# Revit family: Prises non verrouilllées 250 V
name_source: partatom
category: Installations électriques
revit_build: Autodesk Revit 2018 (Build: 20170223_1515(x64)
units: mm (PartAtom-declared; Revit-internal decimal feet)

## family parameters
Conserver l'orientation des annotations = Non
Cote de connecteur circulaire = Utiliser le diamètre
Couper avec des vides une fois chargée = Non
Hôte = Face
Partagée = Non
Point de calcul de pièce = Non
Type d'élément = Normal

## types (9) — shared parameters
Elévation par défaut = 1000 mm  [stored 3.28084 ft]
Fabricant = Legrand
Famille produit = 0854-P17 TEMPRA PRO
Intensité A = 16 A
Prise au standard international pour montage encastré ou saillie avec accessoire permet la connexion d'appareils de puissance = Prise à usage domestique
Température maximum d'utilisation = 40
Température minimum d'utilisation = -25
classe de protection IP = IP54
installation Encastrée E ou Saillie S = encastré
matériau du boitier = plastique
profondeur d'encastrement mm = 26 mm
profondeur mm = 43 mm  [stored 0.141076 ft]
résistance aux chocs IK = 8
sans halogène = Oui
type de raccordement = bornes à vis
zero-valued in all types: Position de la Terre h

## per-type parameters (varying)
| type | Couleur caractéristique | Description | Nombre de pôles | Standard CEI ou NFC | Tension V | entraxe de fixation horizontal mm | entraxe de fixation vertical mm | hauteur mm | largeur mm |
| LG-057676 - P17 - 250 V - 16 A - 2P+T | bleu | LG-057676_Panneau de montage prise P17  250 V - 16 A - 2P+T | 2 | SCHUKO |  | 60 mm | 60 mm | 75 mm | 75 mm |
| LG-057675 - P17 - 250 V - 16 A - 2P+T | blanc | LG-057675_Panneau de montage prise P17 - 250 V - 16 A - 2P+T | 2 | SCHUKO |  | 38 mm | 38 mm | 62 mm | 50 mm  [stored 0.164042 ft] |
| LG-057674 - P17 - IP54 - 250 V - 16 A - 2P+T | blanc | LG-057674_Prise P17 - IP54 - 250 V - 16 A - 2P+T | 2 | SCHUKO |  | 38 mm | 38 mm | 62 mm | 50 mm  [stored 0.164042 ft] |
| LG-057673 - P17 - IP54 - 250 V - 16 A - 2P+T | noir | LG-057673_Prise P17 - IP54 - 250 V - 16 A - 2P+T | 2 | SCHUKO |  | 38 mm | 38 mm | 62 mm | 50 mm  [stored 0.164042 ft] |
| LG-057672 - P17 - 250 V - 16 A - 2P+T | bleu | LG-057672_Panneau de montage prise P17 250 V - 16 A - 2P+T | 3 | SCHUKO | 230 V  50/60 Hz  bleu | 60 mm | 60 mm | 75 mm | 75 mm |
| LG-057671 - P17 - IP54 - 250 V - 16 A - 2P+T | bleu | LG-057671_Prise P17 - IP54 - 250 V - 16 A - 2P+T | 3 | SCHUKO | 230 V  50/60 Hz  bleu | 60 mm | 60 mm | 75 mm | 75 mm |
| LG-057670 - P17 - IP54 - 250 V - 16 A - 2P+T | bleu | LG-057670_Prise P17 - IP54 - 250 V - 16 A - 2P+T | 3 | SCHUKO | 230 V  50/60 Hz  bleu | 38 mm | 38 mm | 50 mm  [stored 0.164042 ft] | 50 mm  [stored 0.164042 ft] |
| LG-057669 - P17 - 250 V - 16 A - 2P+T | blanc | LG-057669_Panneau de montage prise P17 - 250 V - 16 A - 2P+T | 3 | SCHUKO | 230 V  50/60 Hz  bleu | 38 mm | 38 mm | 50 mm  [stored 0.164042 ft] | 50 mm  [stored 0.164042 ft] |
| LG-057667 - P17 - IP54 - 250 V - 16 A - 2P+T | bleu | LG-057667_Prise P17 - IP54 - 250 V - 16 A - 2P+T | 3 | NFC | 230 V  50/60 Hz  bleu | 38 mm | 38 mm | 50 mm  [stored 0.164042 ft] | 50 mm  [stored 0.164042 ft] |

note: [stored X ft] marks values corroborated as IEEE doubles in the binary element streams (Revit-internal decimal feet)
